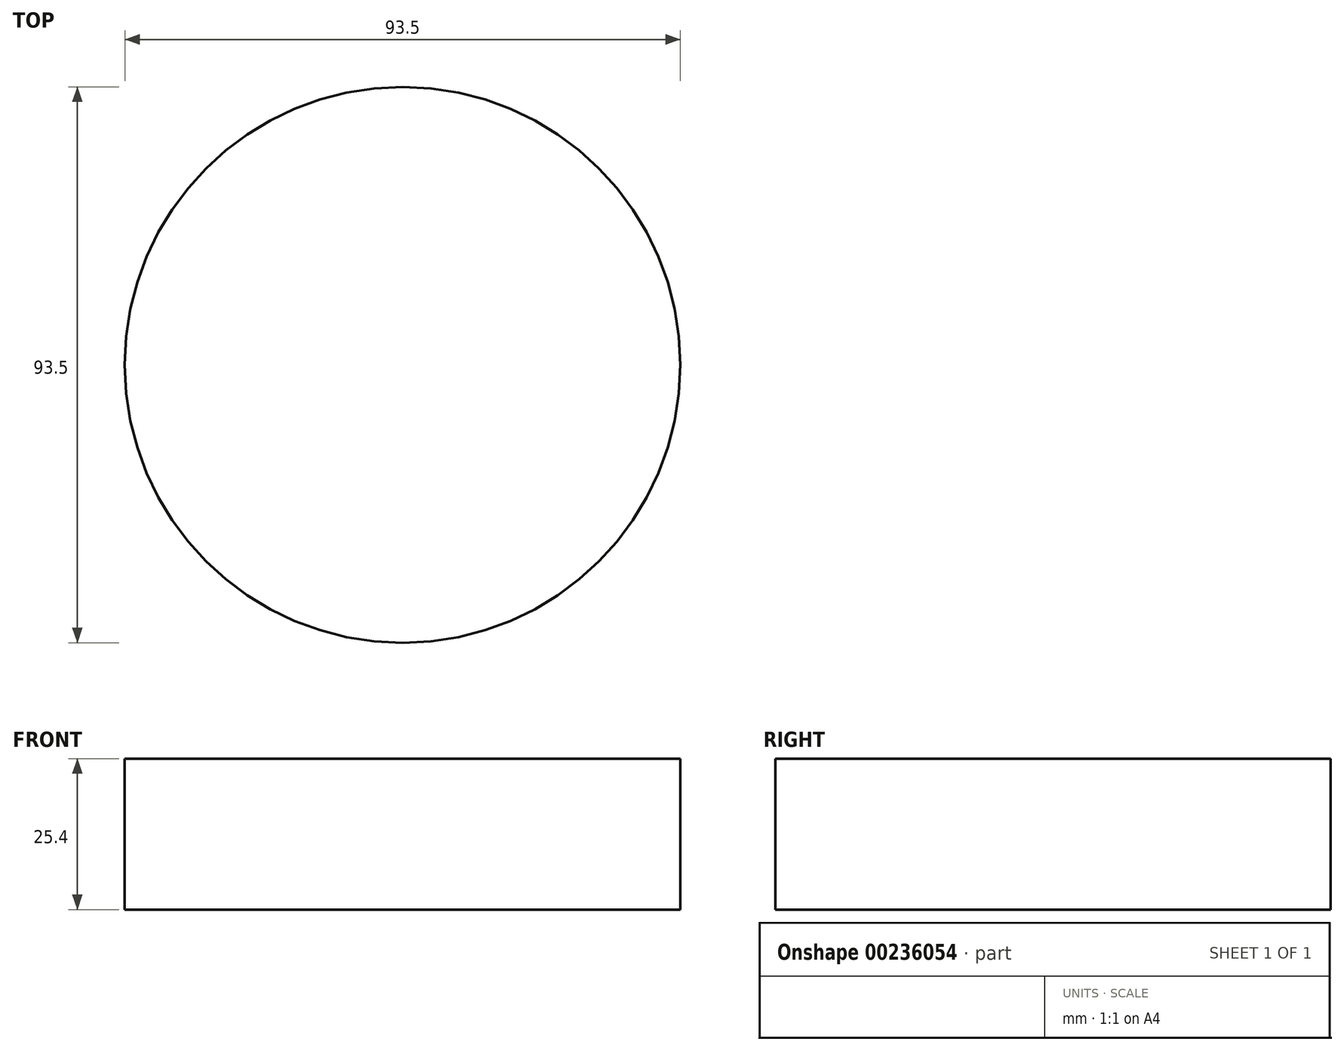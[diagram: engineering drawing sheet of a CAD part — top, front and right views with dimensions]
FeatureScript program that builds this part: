
annotation { "Feature Type Name" : "Feature", "Feature Type Description" : "" }
export const myFeature = defineFeature(function(context is Context, id is Id, definition is map)
    precondition{}
    {
        {
            var Q0;
            Q0=qCreatedBy(makeId("Top.planeOp"),FACE);
            var sketch = newSketch(context, id + "F0", { "sketchPlane" : qUnion([Q0])});
            skCircle(sketch, "E0", {"center": v(0, 0) * mm, "radius": 46.75 * mm});
            skSolve(sketch);
        }
        {
            var Q0;
            Q0=makeQuery(id+"F0.imprint","IMPRINT",FACE,{"disambiguationData":[TD([[makeQuery(id+"F0.imprint","IMPRINT",EDGE,{"derivedFrom":sQuery(id+"F0.wireOp",EDGE,"E0")}),1.0]])]});
            extrude(context, id + "F1", {"entities" : qUnion([Q0]), "depth" : 25.4 * mm});
        }
    });
